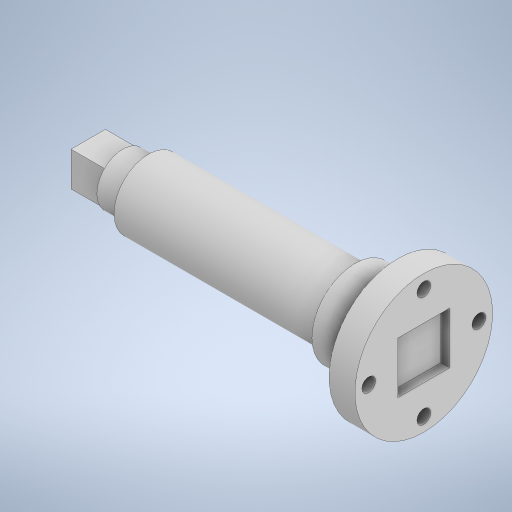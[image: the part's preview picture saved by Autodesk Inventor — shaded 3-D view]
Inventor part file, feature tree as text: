
AUTODESK INVENTOR PART (.ipt)
format: ipt  version: 2023 (Build 270158030, 158C)  size: 292,352 bytes
history: native  units: mm
features: extrude x7, sketch x7
ambient origin geometry x8: Origin, YZ Plane, XZ Plane, XY Plane, X Axis, Y Axis, Z Axis, Center Point
bodies: Solid1 (feature_tree)
feature tree (14):
  extrude  "Extrusion1"  Depth=15.0mm TaperAngle=0.0deg
  extrude  "Extrusion2"  Depth=25.0mm TaperAngle=0.0deg
  extrude  "Extrusion3"  Depth=120.0mm TaperAngle=0.0deg
  extrude  "Extrusion4"  Depth=15.0mm TaperAngle=0.0deg
  extrude  "Extrusion5"  Depth=20.0mm
  extrude  "Extrusion6"  Depth=10.0mm
  extrude  "Extrusion7"  Depth=30.0mm
  sketch  "Sketch1"  dims[d0=80.0mm d1=15.0mm d2=0.0mm]
  sketch  "Sketch2"  dims[d3=50.0mm d4=25.0mm d5=0.0mm]
  sketch  "Sketch3"  dims[d6=40.0mm d7=120.0mm d8=0.0mm]
  sketch  "Sketch4"  dims[d9=30.0mm d10=15.0mm d11=0.0mm]
  sketch  "Sketch5"  dims[d12=20.0mm d13=20.0mm]
  sketch  "Sketch6"  dims[d14=10.0mm d15=10.0mm]
  sketch  "Sketch7"  dims[d16=20.0mm d17=0.0mm d18=30.0mm d19=30.0mm d20=15.0mm d21=15.0mm d22=5.0mm d23=0.0mm d24=64.0mm d25=8.0mm d26=0.0mm d27=0.0mm]
